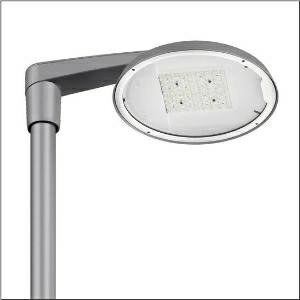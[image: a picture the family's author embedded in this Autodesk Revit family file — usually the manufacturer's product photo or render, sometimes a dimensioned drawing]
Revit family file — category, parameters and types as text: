
# Revit family: dl_50_iq_mini___st0_5a_5xa248b31f08me_ac5a
name_source: partatom
category: Lighting Fixtures
units: mm (PartAtom-declared; Revit-internal decimal feet)

## family parameters
Cut with Voids When Loaded = No
Host = Face
Light Source = No
Part Type = Normal
Room Calculation Point = No
Round Connector Dimension = Use Diameter
Shared = No

## types (1)
- --- (1 x LED, 15660 lm, 107.8 W, 3000K)
    Apparent Load = 108 VA
    CIE Flux Codes = 41 75 97 100 100
    Color Rendering = 70
    Color Temperature = 3000K
    Default Elevation = 1800 mm
    Description = DL 50 iQ mini, mast luminaire, primary light control with lens, of PMMA, primary optical cover: cover, of toughened safety glass, transparent, light distribution: ST0.5a, light emission: direct distribution, primary light characteristic: asymmetric, installation type: side-entry, post-top, LED, High Power LED, rated luminous flux: 15.660lm, luminous efficacy: 145lm/W, light colour: 730, colour temperature: 3000K, control gear: iQ Street-Remote, control: optimised constant luminous flux control (CLO 2.0), Desk-Remote (wireless, voltage-free reading and setting of iQ features in the workshop via application-optimized NFC function/RFID function), Light-Fading, Smart-Wire, Night-Set, Lumen-Switch, Temp-Guard, Auto-Match, Street-Remote, mains connection: 230..240V, AC, 50/60Hz, connection cable pre-assembled, cable length: 10,5m, start of lifetime: 108W, end of service life: 118W, reduction: 47W, luminaire housing, of diecast aluminium, powder-coated, SITECO metallic grey (DB 702S), inclination adjustable: 0°, 5°, 10° (post-top) | 0°, -5°, -10°, -15° (side-entry), please order mast post-top element or mast side-entry element separately, diameter: 500mm, height: 115mm, post-top: for spigot size d x l = 76 x 100mm; with reducer (optional accessory) 60 x 100mm | side-entry: for spigot size d x l = 60 x 100mm; with reducer (optional accessory) 42 x 100mm, mounting height: 4..6m, protection rating (complete): IP66, insulation class (complete): insulation class II (safety insulation), certification: CE, ENEC, ENEC+, VDE, impact resistance: IK08, permissible operating ambient temperature for outdoor applications: -25..+40°C, standard-compliant lighting for roads and squares, packaging unit: 1 piece

Light Distribution: ST0.5a
    Height = 115 mm
    Lamp = 1 x LED
    Lamp Light Flux = 15660 lm
    Lamp Power = 107.8 W
    Lamp count = 1
    Length = 500 mm
    Luminous efficacy = 145 lm/W
    Manufacturer = Siteco
    ModVariant = No
    Model = 5XA248B31F08ME
    Number of Poles = 1
    OnlyDefault = Yes
    Power Factor = 1
    Product Name = DL 50 iQ mini | ST0.5a
    Product group = mast luminaire | pylon top
    ProductGroupID = 6100
    Protection Class = Protection class II
    Protection Degree = IP 66
    RLX_Detail_Level = 1
    RLX_Emergency_Light_Flux = 0 lm
    RLX_Emergency_Type = 0
    RLX_Emergency_Type_DB = No
    RlxData = <blob elided: 128193 chars, md5=d49f481b>
    Socket = socket
    Standby Power = 0 W
    System Light Flux = 15660 lm
    System Power = 108 W
    Type Comments = factory setting: luminous flux: 100 % | dim-lin: 254 | 565 mA
    Type Image = l_1251790.jpg
    URL = http://relux.com
    VarID = @adj_142567
    Voltage = 0 V
    Weight = 0.00 kg
    Width = 0 mm  [stored 0 ft]

note: [stored X ft] marks values corroborated as IEEE doubles in the binary element streams (Revit-internal decimal feet)

## geometry (parser evidence)
native form markers: Blend x4, Sweep x12
no freeform markers — native parametric forms only
